# Revit family: Reece_Laundry Trough_Base_Inset Laundry Trough_Double
name_source: partatom
category: Plumbing Fixtures
revit_build: Autodesk Revit 2018 (Build: 20180329_1100(x64)
units: mm (PartAtom-declared; Revit-internal decimal feet)

## family parameters
Cut with Voids When Loaded = No
Host = Face
Part Type = Normal
Room Calculation Point = Yes
Round Connector Dimension = Use Diameter
Shared = Yes

## types (1)
- 90 Litres_Stainless Steel
    CWFU = 0
    Default Elevation = 0 mm  [stored 0 ft]
    Description = Reece_Laundry Trough_Base_Inset Laundry Trough_Double
    Disclaimer = THIS FILE IS THE PROPERTY OF THE REECE GROUP. IT MAY NOT BE REPRODUCED, REVERSE-ENGINEERED OR MODIFIED. ANY REPUBLICATION, TRANSMISSION OR DISTRIBUTION FOR THE PURPOSE OF COMMERCIALLY EXPLOITING THE FILES IS PROHIBITED.
    HWFU = 0
    Keynote = Product #9504718, Reece_Laundry Trough_Base_Inset Laundry Trough_Double - 90 Litres_Stainless Steel
    Manufacturer = Base
    Model = -
    Reece_Detail_Additional = Double Trough
    Reece_Detail_Disclaimer = THIS FILE IS THE PROPERTY OF THE REECE GROUP. IT MAY NOT BE REPRODUCED, REVERSE-ENGINEERED OR MODIFIED. ANY REPUBLICATION, TRANSMISSION OR DISTRIBUTION FOR THE PURPOSE OF COMMERCIALLY EXPLOITING THE FILES IS PROHIBITED.
    Reece_Material_Main = Reece_Metal_Steel
    Reece_Material_Secondary = Reece_Metal_Steel
    Reece_Overall_Capacity = 90 L
    Reece_Overall_Height = 235 mm
    Reece_Overall_Length = 500 mm
    Reece_Overall_Width = 1160 mm
    Reece_Product_Brand = Base
    Reece_Product_Description = Base Double Inset Laundry Trough 1 Taphole with Bypass 90 litres Stainless Steel
    Reece_Product_Mount = Inset
    Reece_Product_Number = 9504718
    Reece_Product_Sub Brand = -
    Reece_Product_Type = Laundry Trough
    Reece_Product_Web Page = https://www.reece.com.au
    Reece_Sink_Outlet = 40 mm  [stored 0.131234 ft]
    Type Comments = Laundry Trough
    URL = https://www.reece.com.au
    WFU = 0

note: [stored X ft] marks values corroborated as IEEE doubles in the binary element streams (Revit-internal decimal feet)

## geometry (parser evidence)
native form markers: Sweep x2
no freeform markers — native parametric forms only
